# Revit family: Roller_Shades-Lutron-Pocket_Recessed-Roller_100_150_200
name_source: partatom
category: Specialty Equipment
revit_build: Autodesk Revit 2017 (Build: 20160720_1515(x64)
units: mm (PartAtom-declared; Revit-internal decimal feet)

## family parameters
Cut with Voids When Loaded = No
Host = Face
OmniClass Number = 23.30.60.14.21
OmniClass Title = Shades
Part Type = Normal
Room Calculation Point = No
Round Connector Dimension = Use Diameter
Shared = No

## types (3) — shared parameters
Assembly Code = E2010320
Default Elevation = 0' - 0"
Description = Motorized Roller Shade
Fabric Roll Detail = Standard
Instruction Sheet Link = http://www.lutron.com
Manufacturer = Lutron Electronics Co., Inc
Manufacturer Fax Number = 610-282-1243
Mounting = Pocket
Overall Depth = 0' - 4 3/4"
Performance URL = http://www.lutron.com
Product Documentation Link = http://www.lutron.com
Product Name = Motorized Roller Shade - Pocket Mount
Product Page URL = http://www.lutron.com
Series = Sivoia QS
Shade Material = Fabric - Lutron - Linen - White
URL = http://www.lutron.com
Version = 2017 - v1.0b
Video Link = https://www.youtube.com
Warranty URL = http://www.lutron.com
zero-valued in all types: Cost

## per-type parameters (varying)
| type | Maximum Shade Area | Maximum Shade Width | Model |
| Roller 100 - Pocket Mount | 100.00 SF | 10' - 0" | Roller 100 |
| Roller 150 - Pocket Mount | 150.00 SF | 10' - 0" | Roller 150 |
| Roller 200 - Pocket Mount | 200.00 SF | 15' - 0" | Roller 200 |

## geometry (parser evidence)
native form markers: Blend x3, Sweep x2
no freeform markers — native parametric forms only
